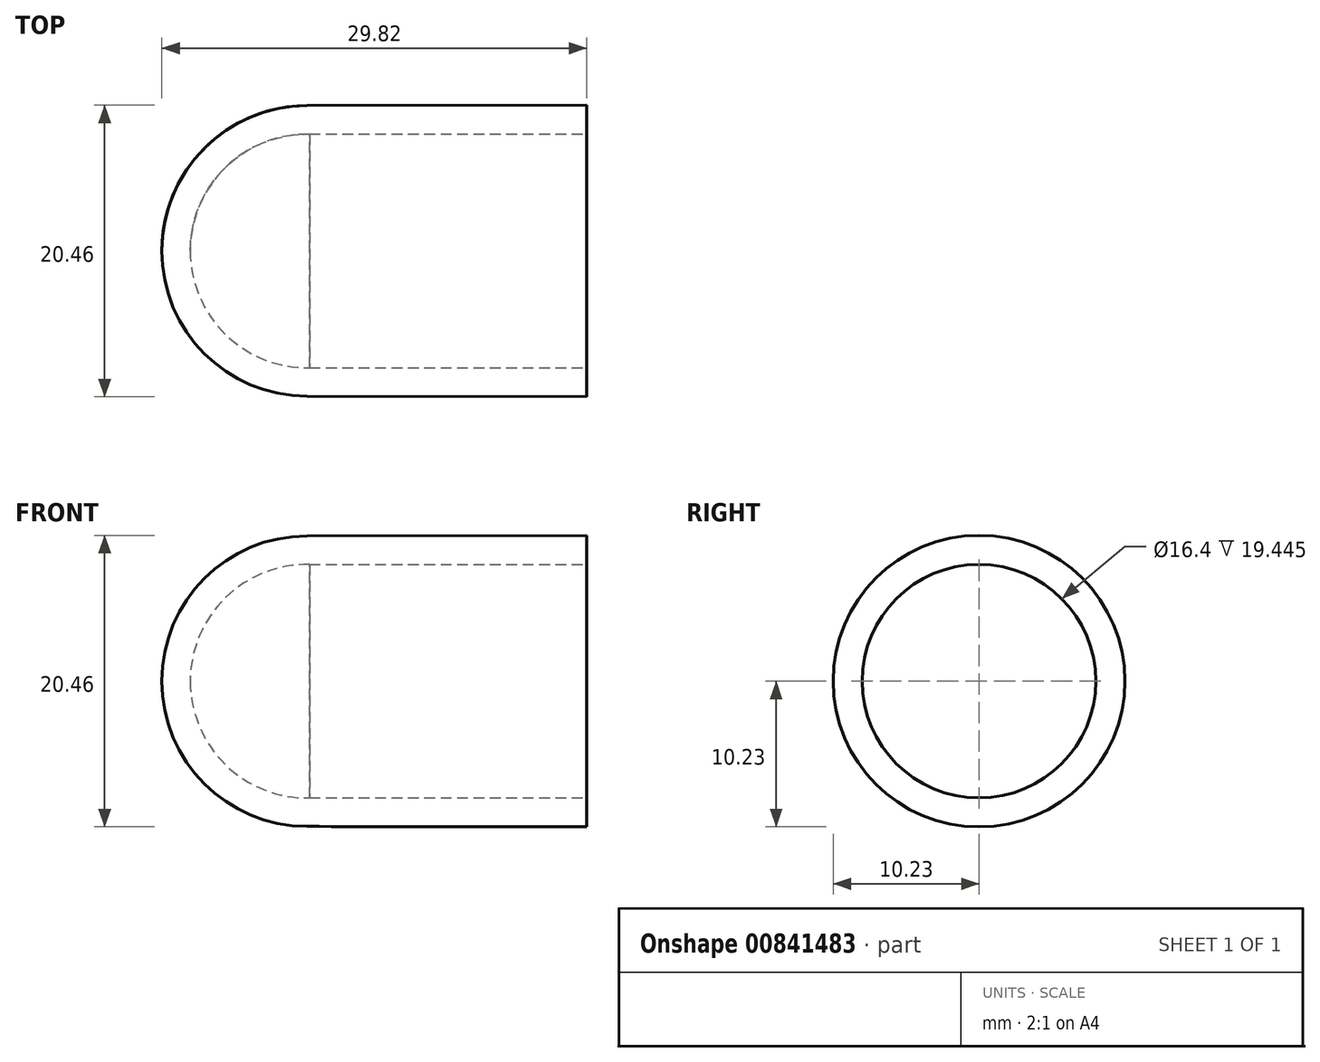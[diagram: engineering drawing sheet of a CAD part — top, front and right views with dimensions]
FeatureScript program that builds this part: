
annotation { "Feature Type Name" : "Feature", "Feature Type Description" : "" }
export const myFeature = defineFeature(function(context is Context, id is Id, definition is map)
    precondition{}
    {
        {
            var Q0;
            Q0=qCreatedBy(makeId("Top.planeOp"),FACE);
            var sketch = newSketch(context, id + "F0", { "sketchPlane" : qUnion([Q0])});
            skArc(sketch, "E0", {"start": v(-0.02, 10.2) * mm, "mid": v(-7.22, 7.2) * mm, "end": v(-10.2, 0) * mm});
            skArc(sketch, "E1", {"start": v(0.17, 8.2) * mm, "mid": v(-5.74, 5.86) * mm, "end": v(-8.2, 0) * mm});
            skLineSegment(sketch, "E2", {"start": v(-0.02, 10.2) * mm, "end": v(-0.02, 10.2) * mm});
            skLineSegment(sketch, "E3", {"start": v(19.62, 10.23) * mm, "end": v(19.62, 8.2) * mm});
            skLineSegment(sketch, "E4", {"start": v(19.62, 8.2) * mm, "end": v(0.17, 8.2) * mm});
            skLineSegment(sketch, "E5", {"start": v(-8.2, 0) * mm, "end": v(-10.2, 0) * mm});
            skArc(sketch, "E6.converted", {"start": v(-10.2, 0) * mm, "mid": v(-4.6, 9.1) * mm, "end": v(6.07, 8.2) * mm});
            skPoint(sketch, "E7.orphan", {"position": v(-10.2, 0) * mm});
            skPoint(sketch, "E8.orphan", {"position": v(-8.2, 0) * mm});
            skLineSegment(sketch, "E9", {"start": v(-0.02, 10.2) * mm, "end": v(19.62, 10.23) * mm});
            skArc(sketch, "E10", {"start": v(-8.2, 0) * mm, "mid": v(-5.74, 5.86) * mm, "end": v(0.17, 8.2) * mm});
            skSolve(sketch);
        }
        {
            var Q0;
            Q0=makeQuery(id+"F0.imprint","IMPRINT",FACE,{"disambiguationData":[TD([[makeQuery(id+"F0.imprint","IMPRINT",EDGE,{"derivedFrom":sQuery(id+"F0.wireOp",EDGE,"E0")}),1.0]])]});
            var Q1;
            {var subQ4=sQuery(id+"F0.wireOp",EDGE,"E5");Q1=makeQuery(id+"F0.imprint","IMPRINT",FACE,{"disambiguationData":[TD([[makeQuery(id+"F0.imprint","IMPRINT",EDGE,{"derivedFrom":subQ4}),-1.0]])]});}
            var Q2;
            {var subQ0=sQuery(id+"F0.wireOp",EDGE,"E3");Q2=makeQuery(id+"F0.imprint","IMPRINT",FACE,{"disambiguationData":[TD([[makeQuery(id+"F0.imprint","IMPRINT",EDGE,{"derivedFrom":subQ0}),-1.0]])]});}
            var Q3;
            Q3=sQuery(id+"F0.wireOp",EDGE,"E5");
            revolve(context, id + "F1", {"surfaceOperationType" : NewSurfaceOperationType.NEW, "entities" : qUnion([Q0, Q1, Q2]), "axis" : qUnion([Q3]), "revolveType" : RevolveType.FULL});
        }
    });
